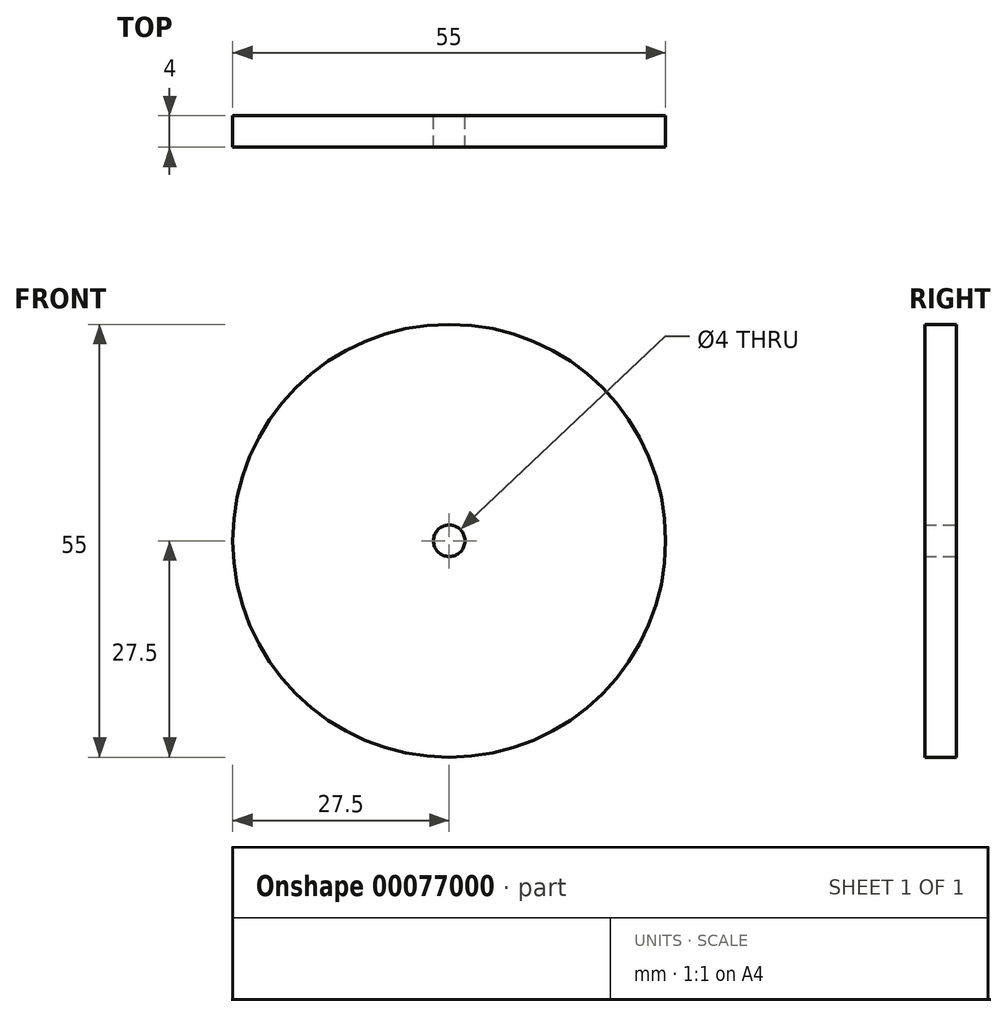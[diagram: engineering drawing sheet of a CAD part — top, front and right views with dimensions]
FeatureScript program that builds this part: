
annotation { "Feature Type Name" : "Feature", "Feature Type Description" : "" }
export const myFeature = defineFeature(function(context is Context, id is Id, definition is map)
    precondition{}
    {
        {
            var Q0;
            Q0=qCreatedBy(makeId("Front.planeOp"),FACE);
            var sketch = newSketch(context, id + "F0", { "sketchPlane" : qUnion([Q0])});
            skCircle(sketch, "E0", {"center": v(0, 0) * mm, "radius": 2 * mm});
            skCircle(sketch, "E1", {"center": v(0, 0) * mm, "radius": 27.5 * mm});
            skSolve(sketch);
        }
        {
            var Q0;
            Q0=makeQuery(id+"F0.imprint","IMPRINT",FACE,{"disambiguationData":[TD([[makeQuery(id+"F0.imprint","IMPRINT",EDGE,{"derivedFrom":sQuery(id+"F0.wireOp",EDGE,"E0")}),-1.0]])]});
            extrude(context, id + "F1", {"entities" : qUnion([Q0]), "depth" : 4 * mm});
        }
    });
